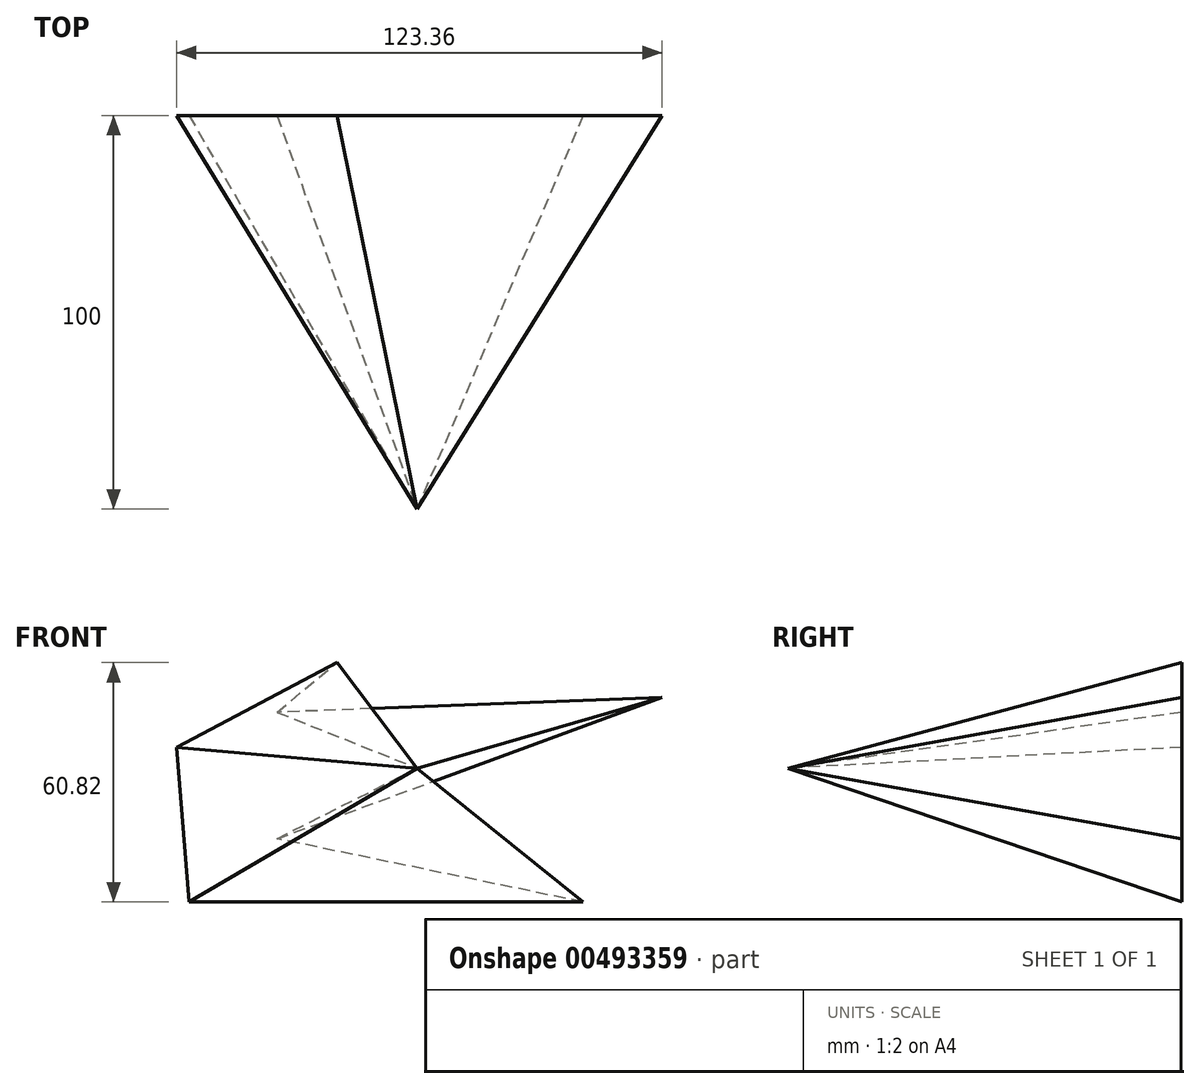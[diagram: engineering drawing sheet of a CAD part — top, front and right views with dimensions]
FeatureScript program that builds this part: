
annotation { "Feature Type Name" : "Feature", "Feature Type Description" : "" }
export const myFeature = defineFeature(function(context is Context, id is Id, definition is map)
    precondition{}
    {
        {
            var Q0;
            Q0=qCreatedBy(makeId("Front.planeOp"),FACE);
            var sketch = newSketch(context, id + "F0", { "sketchPlane" : qUnion([Q0])});
            skLineSegment(sketch, "E0", {"start": v(-20.37, 26.82) * mm, "end": v(-61.1, 5.3) * mm});
            skLineSegment(sketch, "E1", {"start": v(-61.1, 5.3) * mm, "end": v(-57.95, -34) * mm});
            skLineSegment(sketch, "E2", {"start": v(-57.95, -34) * mm, "end": v(42.17, -34) * mm});
            skLineSegment(sketch, "E3", {"start": v(42.17, -34) * mm, "end": v(-35.57, -17.93) * mm});
            skLineSegment(sketch, "E4", {"start": v(-35.57, -17.93) * mm, "end": v(62.25, 17.93) * mm});
            skLineSegment(sketch, "E5", {"start": v(62.25, 17.93) * mm, "end": v(-35.57, 14.2) * mm});
            skLineSegment(sketch, "E6", {"start": v(-35.57, 14.2) * mm, "end": v(-20.37, 26.82) * mm});
            skSolve(sketch);
        }
        {
            var Q0;
            Q0=qCreatedBy(makeId("Front.planeOp"),FACE);
            cPlane(context, id + "F1", {"entities" : qUnion([Q0]), "cplaneType" : CPlaneType.OFFSET, "offset" : 100 * mm, "width" : 150 * mm, "height" : 150 * mm});
        }
        {
            var Q0;
            Q0=qCreatedBy(id+"F1.planeOp",FACE);
            var sketch = newSketch(context, id + "F2", { "sketchPlane" : qUnion([Q0])});
            skPoint(sketch, "E7", {"position": v(0, 0) * mm});
            skSolve(sketch);
        }
        {
            var Q0;
            Q0=makeQuery(id+"F0.imprint","IMPRINT",FACE,{"disambiguationData":[TD([[makeQuery(id+"F0.imprint","IMPRINT",EDGE,{"derivedFrom":sQuery(id+"F0.wireOp",EDGE,"E0")}),1.0]])]});
            var Q1;
            Q1=sQuery(id+"F2.wireOp",VERTEX,"E7");
            loft(context, id + "F3", {"sheetProfilesArray" : [{ "sheetProfileEntities" : qUnion([Q0]) }, { "sheetProfileEntities" : qUnion([Q1]) }]});
        }
    });
